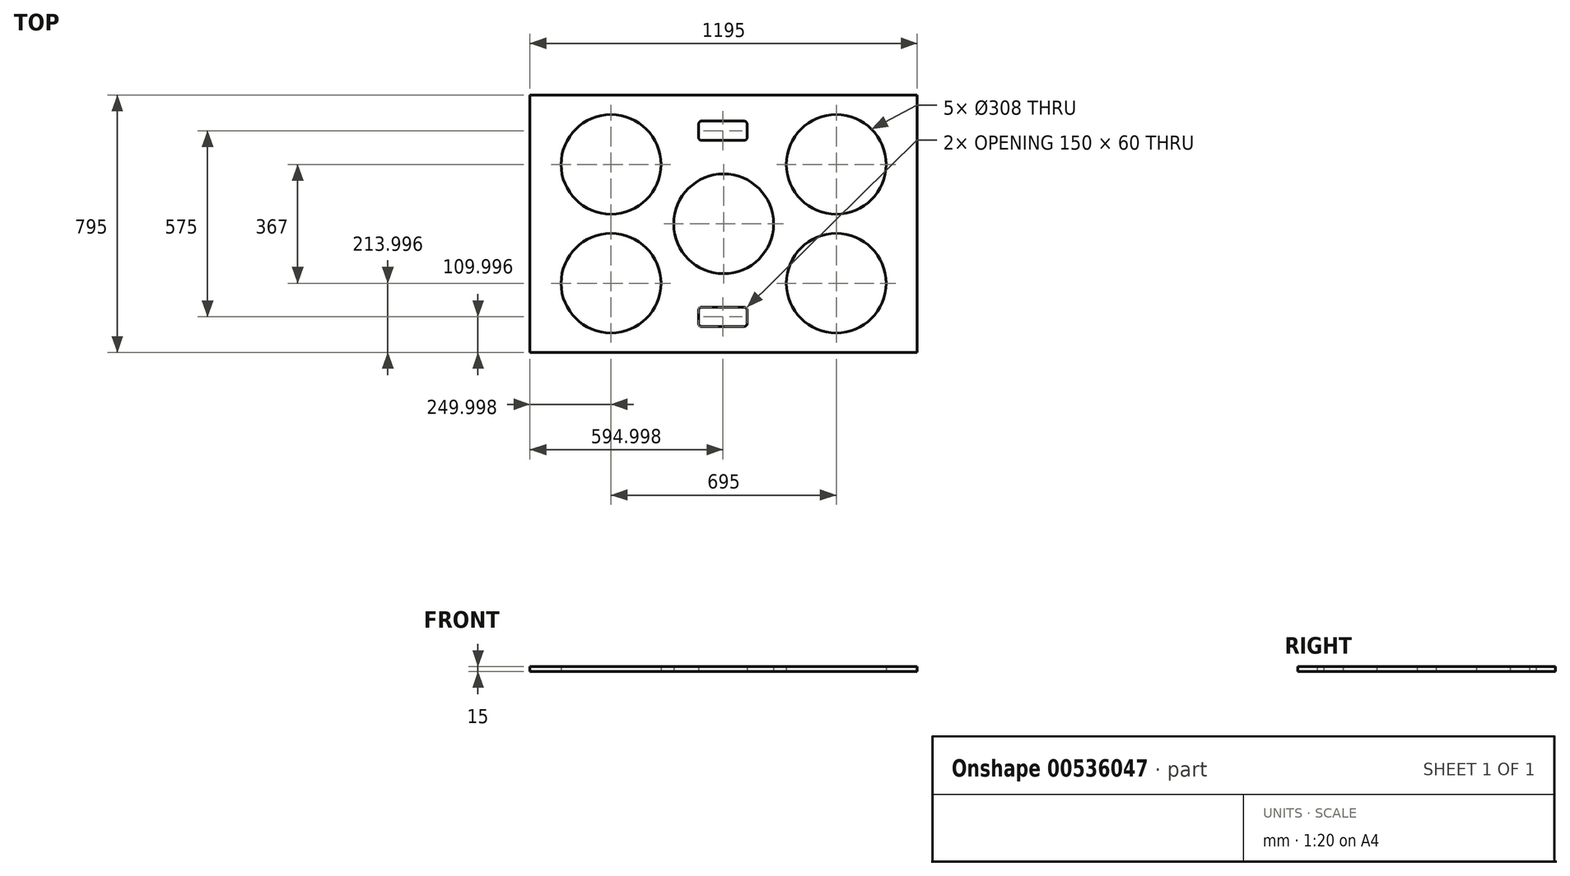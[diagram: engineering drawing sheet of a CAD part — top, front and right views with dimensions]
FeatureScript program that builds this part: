
annotation { "Feature Type Name" : "Feature", "Feature Type Description" : "" }
export const myFeature = defineFeature(function(context is Context, id is Id, definition is map)
    precondition{}
    {
        {
            var Q0;
            Q0=qCreatedBy(makeId("Top.planeOp"),FACE);
            var sketch = newSketch(context, id + "F0", { "sketchPlane" : qUnion([Q0])});
            skPoint(sketch, "E0.visualSharp", {"position": v(1042.48, 508.59) * mm});
            skPoint(sketch, "E1.visualSharp", {"position": v(1042.48, -286.41) * mm});
            skPoint(sketch, "E2.visualSharp", {"position": v(-152.52, -286.41) * mm});
            skCircle(sketch, "E3", {"center": v(97.48, 294.59) * mm, "radius": 154 * mm});
            skCircle(sketch, "E4", {"center": v(97.48, -72.41) * mm, "radius": 154 * mm});
            skCircle(sketch, "E5", {"center": v(444.98, 111.09) * mm, "radius": 154 * mm});
            skCircle(sketch, "E6", {"center": v(792.48, 294.59) * mm, "radius": 154 * mm});
            skCircle(sketch, "E7", {"center": v(792.48, -72.41) * mm, "radius": 154 * mm});
            skLineSegment(sketch, "E8.bottom", {"start": v(1042.48, 508.59) * mm, "end": v(-152.52, 508.59) * mm});
            skLineSegment(sketch, "E8.top", {"start": v(1042.48, -286.41) * mm, "end": v(-152.52, -286.41) * mm});
            skLineSegment(sketch, "E8.left", {"start": v(1042.48, 508.59) * mm, "end": v(1042.48, -286.41) * mm});
            skLineSegment(sketch, "E8.right", {"start": v(-152.52, 508.59) * mm, "end": v(-152.52, -286.41) * mm});
            skLineSegment(sketch, "E9.bottom", {"start": v(377.48, 428.59) * mm, "end": v(507.48, 428.59) * mm});
            skLineSegment(sketch, "E9.top", {"start": v(377.48, 368.59) * mm, "end": v(507.48, 368.59) * mm});
            skLineSegment(sketch, "E9.left", {"start": v(367.48, 418.59) * mm, "end": v(367.48, 378.59) * mm});
            skLineSegment(sketch, "E9.right", {"start": v(517.48, 418.59) * mm, "end": v(517.48, 378.59) * mm});
            skLineSegment(sketch, "E10.bottom", {"start": v(377.48, -146.41) * mm, "end": v(507.48, -146.41) * mm});
            skLineSegment(sketch, "E10.top", {"start": v(377.48, -206.41) * mm, "end": v(507.48, -206.41) * mm});
            skLineSegment(sketch, "E10.left", {"start": v(367.48, -156.41) * mm, "end": v(367.48, -196.41) * mm});
            skLineSegment(sketch, "E10.right", {"start": v(517.48, -156.41) * mm, "end": v(517.48, -196.41) * mm});
            skPoint(sketch, "E11.visualSharp", {"position": v(367.48, 428.59) * mm});
            skArc(sketch, "E11.filletArc", {"start": v(377.48, 428.59) * mm, "mid": v(370.4, 425.66) * mm, "end": v(367.48, 418.59) * mm});
            skPoint(sketch, "E12.visualSharp", {"position": v(367.48, 368.59) * mm});
            skArc(sketch, "E12.filletArc", {"start": v(367.48, 378.59) * mm, "mid": v(370.4, 371.52) * mm, "end": v(377.48, 368.59) * mm});
            skPoint(sketch, "E13.visualSharp", {"position": v(517.48, 368.59) * mm});
            skArc(sketch, "E13.filletArc", {"start": v(507.48, 368.59) * mm, "mid": v(514.55, 371.52) * mm, "end": v(517.48, 378.59) * mm});
            skPoint(sketch, "E14.visualSharp", {"position": v(517.48, 428.59) * mm});
            skArc(sketch, "E14.filletArc", {"start": v(517.48, 418.59) * mm, "mid": v(514.55, 425.66) * mm, "end": v(507.48, 428.59) * mm});
            skPoint(sketch, "E15.visualSharp", {"position": v(517.48, -146.41) * mm});
            skArc(sketch, "E15.filletArc", {"start": v(517.48, -156.41) * mm, "mid": v(514.55, -149.34) * mm, "end": v(507.48, -146.41) * mm});
            skPoint(sketch, "E16.visualSharp", {"position": v(517.48, -206.41) * mm});
            skArc(sketch, "E16.filletArc", {"start": v(507.48, -206.41) * mm, "mid": v(514.55, -203.48) * mm, "end": v(517.48, -196.41) * mm});
            skPoint(sketch, "E17.visualSharp", {"position": v(367.48, -206.41) * mm});
            skArc(sketch, "E17.filletArc", {"start": v(367.48, -196.41) * mm, "mid": v(370.4, -203.48) * mm, "end": v(377.48, -206.41) * mm});
            skPoint(sketch, "E18.visualSharp", {"position": v(367.48, -146.41) * mm});
            skArc(sketch, "E18.filletArc", {"start": v(377.48, -146.41) * mm, "mid": v(370.4, -149.34) * mm, "end": v(367.48, -156.41) * mm});
            skSolve(sketch);
        }
        {
            var Q0;
            Q0=makeQuery(id+"F0.imprint","IMPRINT",FACE,{"disambiguationData":[TD([[makeQuery(id+"F0.imprint","IMPRINT",EDGE,{"derivedFrom":sQuery(id+"F0.wireOp",EDGE,"E3")}),-1.0]])]});
            extrude(context, id + "F1", {"entities" : qUnion([Q0]), "depth" : 15 * mm, "offsetDistance" : 25 * mm});
        }
    });
